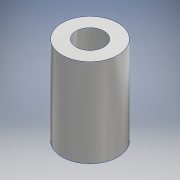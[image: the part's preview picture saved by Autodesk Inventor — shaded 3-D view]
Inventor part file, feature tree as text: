
AUTODESK INVENTOR PART (.ipt)
format: ipt  version: 2016 (Build 200138000, 138)  size: 105,472 bytes
history: native  units: mm
features: other x1, extrude x1, sketch x1
ambient origin geometry x8: Origin, YZ Plane, XZ Plane, XY Plane, X Axis, Y Axis, Z Axis, Center Point
bodies: Body1 (feature_tree)
feature tree (3):
  other  "ソリッド1"
  extrude  "押し出し1"  Depth=6.0mm
  sketch  "スケッチ1"
